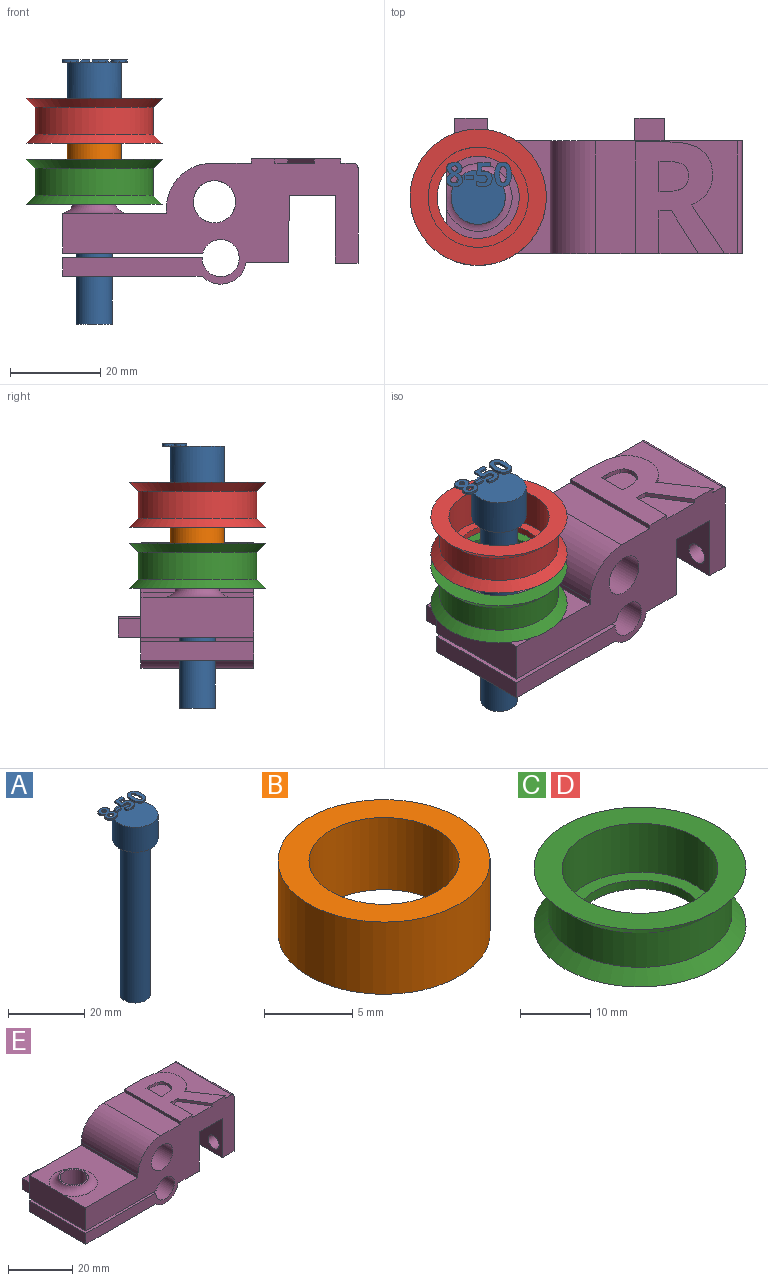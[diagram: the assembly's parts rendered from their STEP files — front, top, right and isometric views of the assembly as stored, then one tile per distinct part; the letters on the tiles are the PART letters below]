
ASSEMBLY  parts=5 mates=4
PART A: 86 faces, bbox 14.5x13.7x58.5 mm
  f0: plane 12x12mm, normal (0,0,1), area 99.4mm2, adj f5,f22,f23,f24,f25,f26,f40,f41
  f1: plane 1x0.26mm, normal (0,0,1), area 0.1mm2, adj f5,f46,f47,f48,f49
  f2: plane 0.85x0.68mm, normal (0,0,1), area 0.2mm2, adj f5,f29,f30,f31
  f3: cylinder r=4mm len=50mm, axis (0,0,-1), area 1256.6mm2, adj f4,f6
  f4: plane 8x8mm, normal (0,0,-1), area 50.3mm2, adj f3
  f5: cylinder r=6mm len=12mm, axis (0,0,-1), area 301.6mm2, adj f0,f1,f2,f6,f39,f45,f67,f85
  f6: plane 12x12mm, normal (0,0,-1), area 62.8mm2, adj f3,f5
  f7: extruded ~0.5x0.46mm, area 0.2mm2, adj f8,f37,f38,f39
  f8: extruded ~0.5x0.46mm, area 0.2mm2, adj f7,f9,f38,f39
  f9: extruded ~0.5x0.39mm, area 0.2mm2, adj f8,f10,f38,f39
  f10: extruded ~0.5x0.4mm, area 0.2mm2, adj f9,f11,f38,f39
  f11: extruded ~0.5x0.49mm, area 0.3mm2, adj f10,f12,f38,f39
  f12: extruded ~0.5x0.5mm, area 0.3mm2, adj f11,f13,f38,f39
  f13: extruded ~0.5x0.39mm, area 0.2mm2, adj f12,f37,f38,f39
  f14: extruded ~1.22x0.5mm, area 0.6mm2, adj f15,f35,f38,f39
  f15: extruded ~1.22x0.5mm, area 0.6mm2, adj f14,f16,f38,f39
  f16: extruded ~0.91x0.5mm, area 0.5mm2, adj f15,f17,f38,f39
  f17: extruded ~0.71x0.5mm, area 0.4mm2, adj f16,f18,f38,f39
  f18: extruded ~0.65x0.61mm, area 0.4mm2, adj f17,f19,f38,f39
  f19: extruded ~0.77x0.62mm, area 0.5mm2, adj f18,f20,f38,f39
  f20: extruded ~0.8x0.5mm, area 0.4mm2, adj f19,f21,f38,f39
  f21: extruded ~1.04x0.5mm, area 0.6mm2, adj f20,f22,f38,f39
  f22: extruded ~1.36x0.5mm, area 0.7mm2, adj f0,f21,f23,f38,f39
  f23: extruded ~1.33x0.5mm, area 0.7mm2, adj f0,f22,f24,f38
  f24: extruded ~1.04x0.51mm, area 0.6mm2, adj f0,f23,f25,f38
  f25: extruded ~0.75x0.5mm, area 0.4mm2, adj f0,f24,f26,f38
  f26: extruded ~0.85x0.66mm, area 0.5mm2, adj f0,f25,f27,f38,f39
  f27: extruded ~0.72x0.56mm, area 0.5mm2, adj f26,f28,f38,f39
  f28: extruded ~0.72x0.5mm, area 0.4mm2, adj f27,f35,f38,f39
  f29: extruded ~0.5x0.45mm, area 0.3mm2, adj f2,f30,f36,f38,f39
  f30: extruded ~0.5x0.47mm, area 0.3mm2, adj f2,f29,f31,f38
  f31: extruded ~0.62x0.5mm, area 0.3mm2, adj f2,f30,f32,f38,f39
  f32: extruded ~0.59x0.5mm, area 0.3mm2, adj f31,f33,f38,f39
  f33: extruded ~0.5x0.48mm, area 0.3mm2, adj f32,f34,f38,f39
  f34: extruded ~0.89x0.77mm, area 0.6mm2, adj f33,f36,f38,f39
  f35: extruded ~0.93x0.5mm, area 0.5mm2, adj f14,f28,f38,f39
  f36: extruded ~0.66x0.5mm, area 0.4mm2, adj f29,f34,f38,f39
  f37: extruded ~0.5x0.39mm, area 0.2mm2, adj f7,f13,f38,f39
  f38: plane 5.4x3.69mm, normal (0,0,1), area 12.7mm2, adj f7,f8,f9,f10,f11,f12,f13,f14
  f39: plane 5.4x3.53mm, normal (0,0,-1), area 10.2mm2, adj f5,f7,f8,f9,f10,f11,f12,f13
  f40: plane 0.9x0.5mm, normal (-1,0,0), area 0.4mm2, adj f0,f41,f43,f44
  f41: plane 1.93x0.5mm, normal (0,-1,0), area 1mm2, adj f0,f40,f42,f44
  f42: plane 0.9x0.5mm, normal (1,0,0), area 0.4mm2, adj f0,f41,f43,f44
  f43: plane 1.93x0.5mm, normal (0,1,0), area 1mm2, adj f0,f40,f42,f44
  f44: plane 1.93x0.9mm, normal (0,0,1), area 1.7mm2, adj f40,f41,f42,f43
  f45: plane 0.76x0.31mm, normal (0,0,-1), area 0mm2, adj f5,f46
  f46: extruded ~1.21x0.5mm, area 0.7mm2, adj f0,f1,f45,f47,f65,f66
  f47: extruded ~0.54x0.5mm, area 0.3mm2, adj f1,f46,f48,f66
  f48: plane 0.5x0.13mm, normal (-0.2,0.98,0), area 0.1mm2, adj f1,f47,f49,f66
  f49: plane 1.03x0.5mm, normal (1,-0.09,0), area 0.5mm2, adj f1,f48,f50,f66,f67
  f50: plane 1.88x0.5mm, normal (0,-1,0), area 0.9mm2, adj f49,f51,f66,f67
  f51: plane 0.94x0.5mm, normal (1,0,0), area 0.5mm2, adj f50,f52,f66,f67
  f52: plane 2.85x0.5mm, normal (0,1,0), area 1.4mm2, adj f51,f53,f66,f67
  f53: plane 2.68x0.5mm, normal (-1,0.07,0), area 1.3mm2, adj f0,f52,f54,f66,f67
  f54: plane 0.5x0.44mm, normal (-0.47,-0.88,0), area 0.3mm2, adj f0,f53,f55,f66
  f55: extruded ~0.5x0.37mm, area 0.2mm2, adj f0,f54,f56,f66
  f56: extruded ~0.5x0.42mm, area 0.2mm2, adj f0,f55,f57,f66
  f57: extruded ~1.05x0.8mm, area 0.8mm2, adj f0,f56,f58,f66
  f58: extruded ~1.02x0.83mm, area 0.8mm2, adj f0,f57,f59,f66
  f59: extruded ~0.72x0.5mm, area 0.4mm2, adj f0,f58,f60,f66
  f60: extruded ~0.66x0.5mm, area 0.4mm2, adj f0,f59,f61,f66
  f61: plane 0.96x0.5mm, normal (-1,0,0), area 0.5mm2, adj f0,f60,f62,f66
  f62: extruded ~1.42x0.5mm, area 0.7mm2, adj f0,f61,f63,f66
  f63: extruded ~1.55x0.5mm, area 0.8mm2, adj f0,f62,f64,f66
  f64: extruded ~1.36x0.54mm, area 0.8mm2, adj f0,f63,f65,f66
  f65: extruded ~1.17x0.5mm, area 0.6mm2, adj f0,f46,f64,f66
  f66: plane 5.33x3.51mm, normal (0,0,1), area 10.9mm2, adj f46,f47,f48,f49,f50,f51,f52,f53
  f67: plane 2.97x1.71mm, normal (0,0,-1), area 3.5mm2, adj f5,f49,f50,f51,f52,f53
  f68: extruded ~1.39x0.5mm, area 0.7mm2, adj f69,f83,f84,f85
  f69: extruded ~1.39x0.5mm, area 0.7mm2, adj f68,f70,f84,f85
  f70: extruded ~0.56x0.5mm, area 0.4mm2, adj f69,f71,f84,f85
  f71: extruded ~0.56x0.5mm, area 0.4mm2, adj f70,f72,f84,f85
  f72: extruded ~1.39x0.5mm, area 0.7mm2, adj f71,f73,f84,f85
  f73: extruded ~1.38x0.5mm, area 0.7mm2, adj f72,f74,f84,f85
  f74: extruded ~0.56x0.5mm, area 0.4mm2, adj f73,f83,f84,f85
  f75: extruded ~2.04x0.5mm, area 1.1mm2, adj f76,f82,f84,f85
  f76: extruded ~2.02x0.5mm, area 1.1mm2, adj f75,f77,f84,f85
  f77: extruded ~1.38x0.69mm, area 0.8mm2, adj f76,f78,f84,f85
  f78: extruded ~1.38x0.66mm, area 0.8mm2, adj f77,f79,f84,f85
  f79: extruded ~2.05x0.5mm, area 1.1mm2, adj f78,f80,f84,f85
  f80: extruded ~2.02x0.5mm, area 1mm2, adj f0,f79,f81,f84,f85
  f81: extruded ~1.37x0.68mm, area 0.8mm2, adj f0,f80,f82,f84
  f82: extruded ~1.39x0.66mm, area 0.8mm2, adj f0,f75,f81,f84,f85
  f83: extruded ~0.56x0.5mm, area 0.4mm2, adj f68,f74,f84,f85
  f84: plane 5.41x3.68mm, normal (0,0,1), area 12.1mm2, adj f68,f69,f70,f71,f72,f73,f74,f75
  f85: plane 5.41x3.68mm, normal (0,0,-1), area 10.3mm2, adj f5,f68,f69,f70,f71,f72,f73,f74
PART B: 4 faces, bbox 12x12x5 mm
  f0: cylinder r=4.25mm len=8.5mm, axis (0,0,-1), area 133.5mm2, adj f2,f3
  f1: cylinder r=6mm len=12mm, axis (0,0,-1), area 188.5mm2, adj f2,f3
  f2: plane 12x12mm, normal (0,0,1), area 56.4mm2, adj f0,f1
  f3: plane 12x12mm, normal (0,0,-1), area 56.4mm2, adj f0,f1
PART C: 8 faces, bbox 30.2x30.2x10 mm
  f0: plane 30.2x30.2mm, normal (0,0,1), area 329.2mm2, adj f1,f7
  f1: cylinder r=11.1mm len=22.2mm, axis (0,0,-1), area 592.8mm2, adj f0,f2
  f2: plane 22.2x22.2mm, normal (0,0,1), area 126.9mm2, adj f1,f3
  f3: cylinder r=9.1mm len=18.2mm, axis (0,0,-1), area 85.8mm2, adj f2,f4
  f4: plane 30.2x30.2mm, normal (0,0,-1), area 456.2mm2, adj f3,f5
  f5: cone r=13.1mm half-angle=45deg, axis (0,0,-1), area 250.6mm2, adj f4,f6
  f6: cylinder r=13.1mm len=26.2mm, axis (0,0,-1), area 493.9mm2, adj f5,f7
  f7: cone r=15.1mm half-angle=45deg, axis (0,0,1), area 250.6mm2, adj f0,f6
PART D: same geometry as C
PART E: 56 faces, bbox 68.9x30x27.7 mm
  f0: plane 31.42x25mm, normal (0,0,1), area 392.1mm2, adj f14,f15,f25,f27,f40,f41,f42,f43
  f1: plane 9.51x8.71mm, normal (0,0,1), area 54.7mm2, adj f14,f37,f38,f39
  f2: plane 25x4.12mm, normal (-1,0,0), area 103mm2, adj f5,f14,f15,f19
  f3: cylinder r=4.17mm len=8.35mm, axis (0,0,1), area 108.1mm2, adj f5,f19
  f4: plane 25x9.34mm, normal (0,0,-1), area 233.4mm2, adj f13,f14,f15,f17
  f5: plane 30.88x25mm, normal (0,0,-1), area 717.2mm2, adj f2,f3,f14,f15,f17
  f6: plane 25x8.82mm, normal (-1,0,0), area 219.6mm2, adj f7,f14,f15,f20,f24
  f7: plane 25x23mm, normal (0,0,1), area 400mm2, adj f6,f8,f14,f15,f24
  f8: plane 25x1.1mm, normal (-1,0,0), area 27.5mm2, adj f7,f14,f15,f25
  f9: plane 25x21.09mm, normal (1,0,0), area 493.5mm2, adj f10,f14,f15,f22,f23,f27
  f10: plane 25x5mm, normal (0,0,-1), area 125mm2, adj f9,f11,f14,f15
  f11: plane 25x15mm, normal (-1,0,0), area 341.3mm2, adj f10,f12,f14,f15,f22,f23
  f12: plane 25x10.2mm, normal (0,0,-1), area 255mm2, adj f11,f13,f14,f15
  f13: plane 25x14.91mm, normal (1,0,-0.01), area 372.8mm2, adj f4,f12,f14,f15
  f14: plane 65.42x27.75mm, normal (0,-1,0), area 997.9mm2, adj f0,f1,f2,f4,f5,f6,f7,f8
  f15: plane 65.42x26.75mm, normal (0,1,0), area 926.8mm2, adj f0,f2,f4,f5,f6,f7,f8,f9
  f16: cylinder r=4.17mm len=10.78mm, axis (0,0,1), area 282.8mm2, adj f20,f21
  f17: cylinder r=5.75mm len=25mm, axis (0,-1,0), area 315.9mm2, adj f4,f5,f14,f15
  f18: cylinder r=4.1mm len=25mm, axis (0,-1,0), area 618.7mm2, adj f14,f15,f19,f20
  f19: plane 30.91x25mm, normal (0,0,1), area 718.1mm2, adj f2,f3,f14,f15,f18
  f20: plane 31.07x30mm, normal (0,0,-1), area 758.4mm2, adj f6,f14,f15,f16,f18,f29,f30,f31
  f21: plane 9.35x9.35mm, normal (0,0,1), area 13.9mm2, adj f16,f24
  f22: cylinder r=2.43mm len=5mm, axis (1,0,0), area 76.2mm2, adj f9,f11
  f23: cylinder r=2.2mm len=5mm, axis (1,0,0), area 69.1mm2, adj f9,f11
  f24: torus R=7.5mm, axis (0,0,-1), area 134.6mm2, adj f6,f7,f21
  f25: cylinder r=10mm len=25mm, axis (0,-1,0), area 392.7mm2, adj f0,f8,f14,f15
  f26: cylinder r=4.68mm len=25mm, axis (0,-1,0), area 735.2mm2, adj f14,f15
  f27: cylinder r=1mm len=25mm, axis (0,-1,0), area 39.3mm2, adj f0,f9,f14,f15
  f28: plane 7.3x5mm, normal (0,0,1), area 36.5mm2, adj f15,f29,f30,f31
  f29: plane 5x4.12mm, normal (-1,0,0), area 20.6mm2, adj f15,f20,f28,f31
  f30: plane 5x4.12mm, normal (1,0,0), area 20.6mm2, adj f15,f20,f28,f31
  f31: plane 7.3x4.12mm, normal (0,1,0), area 30.1mm2, adj f20,f28,f29,f30
  f32: plane 6.63x5mm, normal (0,0,1), area 33.2mm2, adj f15,f33,f35,f36
  f33: plane 5x4.5mm, normal (-1,0,0), area 22.5mm2, adj f15,f32,f34,f36
  f34: plane 6.63x5mm, normal (0,0,-1), area 33.2mm2, adj f15,f33,f35,f36
  f35: plane 5x4.5mm, normal (1,0,0), area 22.5mm2, adj f15,f32,f34,f36
  f36: plane 6.63x4.5mm, normal (0,1,0), area 29.9mm2, adj f32,f33,f34,f35
  f37: plane 9.51x1mm, normal (1,0,0), area 9.5mm2, adj f1,f14,f38,f54
  f38: plane 2.79x1mm, normal (0,-1,0), area 2.8mm2, adj f1,f37,f39,f54
  f39: plane 9.51x5.92mm, normal (-0.85,-0.53,0), area 11.2mm2, adj f1,f14,f38,f54
  f40: extruded ~10.8x7.29mm, area 13mm2, adj f0,f14,f41,f54
  f41: extruded ~3.41x2.67mm, area 4.4mm2, adj f0,f40,f42,f54
  f42: extruded ~3.89x1.2mm, area 4.1mm2, adj f0,f41,f43,f54
  f43: extruded ~5.59x2.42mm, area 6.3mm2, adj f0,f42,f44,f54
  f44: extruded ~7.48x1.84mm, area 7.8mm2, adj f0,f43,f45,f54
  f45: plane 7.22x1mm, normal (0,1,0), area 7.2mm2, adj f0,f44,f46,f54
  f46: plane 24.79x1mm, normal (-1,0,0), area 24.8mm2, adj f0,f14,f45,f54
  f47: plane 1.69x1mm, normal (0,1,0), area 1.7mm2, adj f48,f53,f54,f55
  f48: plane 6.7x1mm, normal (1,0,0), area 6.7mm2, adj f47,f49,f54,f55
  f49: plane 1.6x1mm, normal (0,-1,0), area 1.6mm2, adj f48,f50,f54,f55
  f50: extruded ~3.75x1mm, area 3.9mm2, adj f49,f51,f54,f55
  f51: extruded ~2.51x1.21mm, area 2.9mm2, adj f50,f52,f54,f55
  f52: extruded ~2.61x1.19mm, area 3mm2, adj f51,f53,f54,f55
  f53: extruded ~3.68x1mm, area 3.8mm2, adj f47,f52,f54,f55
  f54: plane 24.79x19.8mm, normal (0,0,1), area 300mm2, adj f14,f37,f38,f39,f40,f41,f42,f43
  f55: plane 6.7x6.56mm, normal (0,0,1), area 38.8mm2, adj f47,f48,f49,f50,f51,f52,f53
PLACE A t=(-110.34,-4.12,-11.8)mm
PLACE B rot(axis=(1,0,0),180deg) t=(-110.34,-4.12,28.2)mm
PLACE C t=(-110.34,-4.12,19.9)mm
PLACE D t=(-110.34,-4.12,33.4)mm
PLACE E t=(-6.56,8.38,1.8)mm
MATE fastened A.f3 <-> D.f1  axis (0,0,-1) through (-110.34,-4.12,38.2)mm
MATE fastened B.f0 <-> C.f1  axis (0,0,1) through (-110.34,-4.12,23.2)mm
MATE fastened C.f1 <-> E.f3  axis (0,0,-1) through (-110.34,-4.12,14.7)mm
MATE fastened D.f1 <-> B.f0  axis (0,0,-1) through (-110.34,-4.12,28.2)mm
